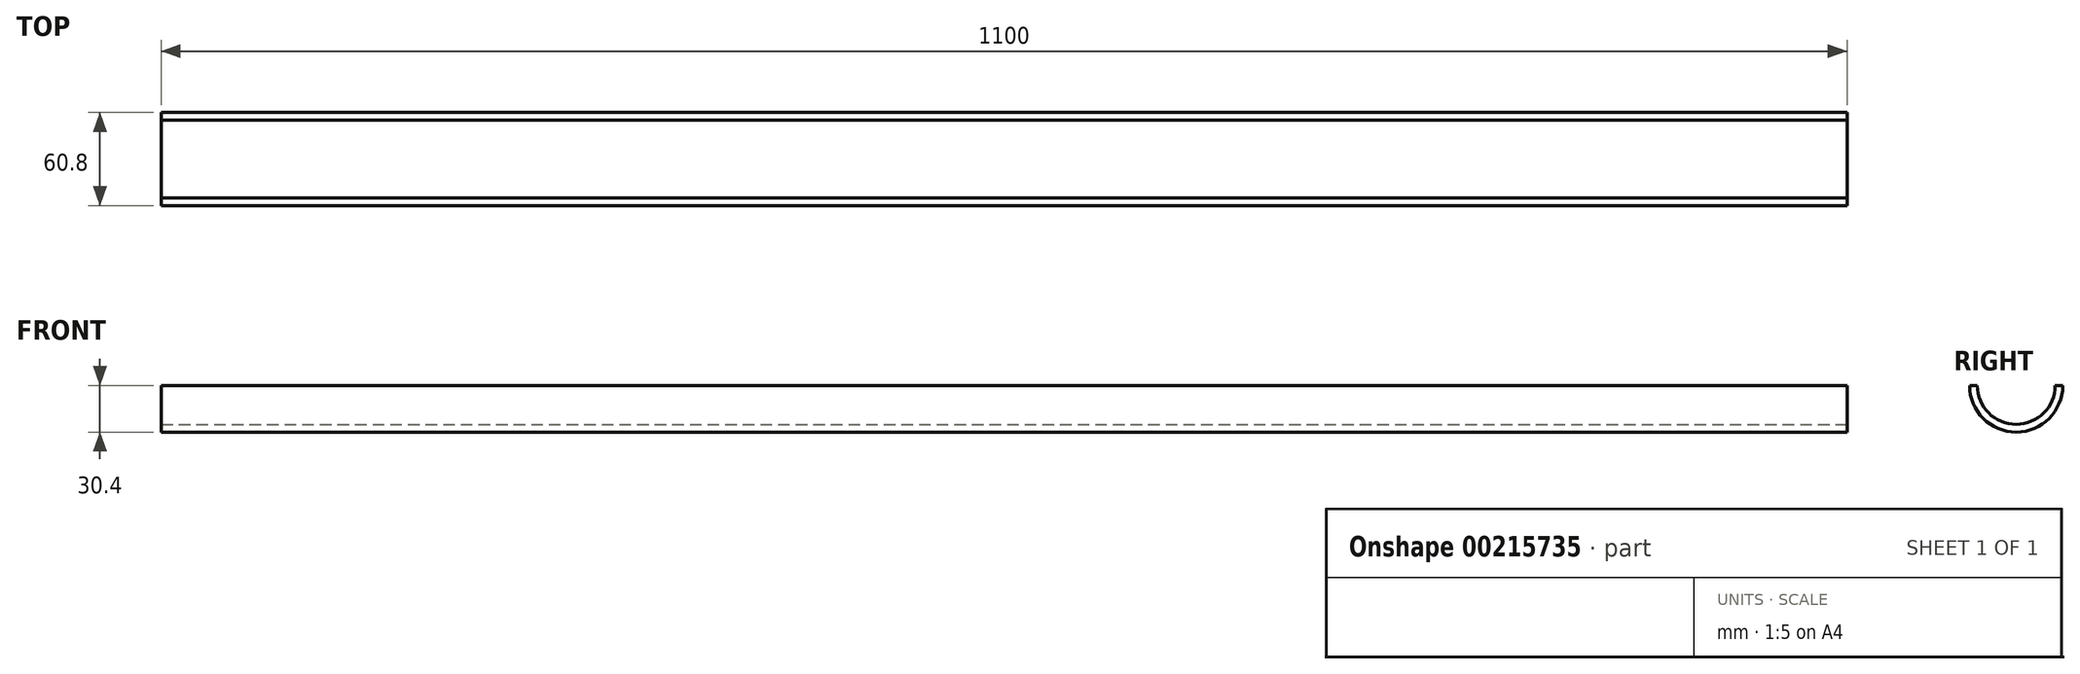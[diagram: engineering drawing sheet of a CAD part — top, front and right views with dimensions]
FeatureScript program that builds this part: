
annotation { "Feature Type Name" : "Feature", "Feature Type Description" : "" }
export const myFeature = defineFeature(function(context is Context, id is Id, definition is map)
    precondition{}
    {
        {
            var Q0;
            Q0=qCreatedBy(makeId("Right.planeOp"),FACE);
            var sketch = newSketch(context, id + "F0", { "sketchPlane" : qUnion([Q0])});
            skArc(sketch, "E0", {"start": v(-25.4, 0) * mm, "mid": v(0, -25.4) * mm, "end": v(25.4, 0) * mm});
            skArc(sketch, "E1.0", {"start": v(-30.4, 0) * mm, "mid": v(0, -30.4) * mm, "end": v(30.4, 0) * mm});
            skLineSegment(sketch, "E2", {"start": v(-25.4, 0) * mm, "end": v(-30.4, 0) * mm});
            skLineSegment(sketch, "E3", {"start": v(30.4, 0) * mm, "end": v(25.4, 0) * mm});
            skSolve(sketch);
        }
        {
            var Q0;
            Q0=makeQuery(id+"F0.imprint","IMPRINT",FACE,{"disambiguationData":[TD([[makeQuery(id+"F0.imprint","IMPRINT",EDGE,{"derivedFrom":sQuery(id+"F0.wireOp",EDGE,"E0")}),-1.0]])]});
            extrude(context, id + "F1", {"entities" : qUnion([Q0]), "oppositeDirection" : true, "depth" : 1100 * mm});
        }
    });
